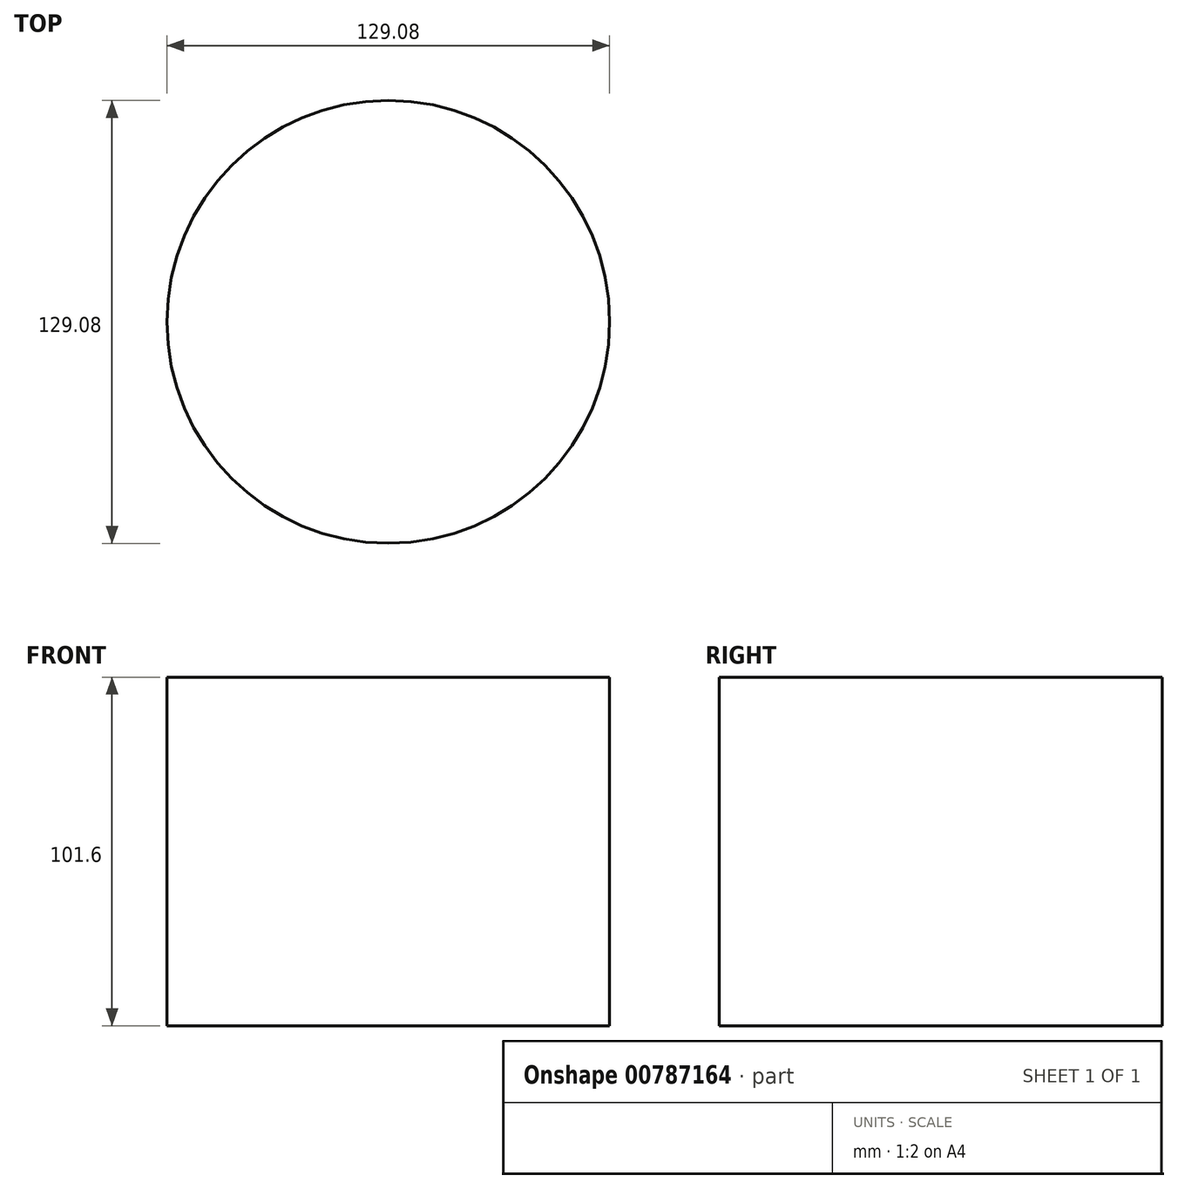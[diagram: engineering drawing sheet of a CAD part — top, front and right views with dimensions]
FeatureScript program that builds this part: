
annotation { "Feature Type Name" : "Feature", "Feature Type Description" : "" }
export const myFeature = defineFeature(function(context is Context, id is Id, definition is map)
    precondition{}
    {
        {
            var Q0;
            Q0=qCreatedBy(makeId("Top.planeOp"),FACE);
            var sketch = newSketch(context, id + "F0", { "sketchPlane" : qUnion([Q0])});
            skCircle(sketch, "E0", {"center": v(0, 0) * mm, "radius": 64.54 * mm});
            skSolve(sketch);
        }
        {
            var Q0;
            Q0=makeQuery(id+"F0.imprint","IMPRINT",FACE,{"disambiguationData":[TD([[makeQuery(id+"F0.imprint","IMPRINT",EDGE,{"derivedFrom":sQuery(id+"F0.wireOp",EDGE,"E0")}),1.0]])]});
            var Q1;
            Q1 = qSketchRegion(id + "F0", true);
            extrude(context, id + "F1", {"entities" : qUnion([Q0, Q1]), "depth" : 101.6 * mm, "offsetDistance" : 25.4 * mm});
        }
    });
